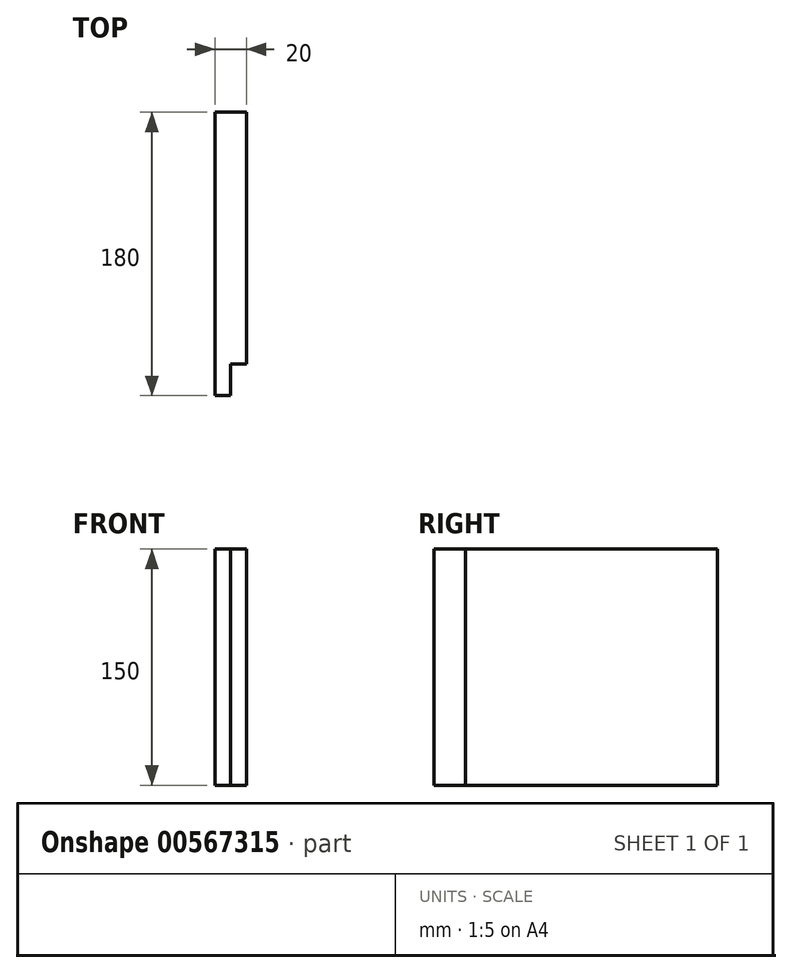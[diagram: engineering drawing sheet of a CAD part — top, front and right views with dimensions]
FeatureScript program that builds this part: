
annotation { "Feature Type Name" : "Feature", "Feature Type Description" : "" }
export const myFeature = defineFeature(function(context is Context, id is Id, definition is map)
    precondition{}
    {
        {
            var Q0;
            Q0=qCreatedBy(makeId("Right.planeOp"),FACE);
            var sketch = newSketch(context, id + "F0", { "sketchPlane" : qUnion([Q0])});
            skLineSegment(sketch, "E0.bottom", {"start": v(-83.42, 106.9) * mm, "end": v(96.58, 106.9) * mm});
            skLineSegment(sketch, "E0.top", {"start": v(-83.42, -43.1) * mm, "end": v(96.58, -43.1) * mm});
            skLineSegment(sketch, "E0.left", {"start": v(-83.42, 106.9) * mm, "end": v(-83.42, -43.1) * mm});
            skLineSegment(sketch, "E0.right", {"start": v(96.58, 106.9) * mm, "end": v(96.58, -43.1) * mm});
            skSolve(sketch);
        }
        {
            var Q0;
            Q0 = qSketchRegion(id + "F0", true);
            extrude(context, id + "F1", {"entities" : qUnion([Q0]), "depth" : 20 * mm, "offsetDistance" : 25 * mm});
        }
        {
            var Q0;
            Q0=makeQuery(id+"F1.opExtrude","SWEPT_FACE",FACE,{"disambiguationData":[OSD([sQuery(id+"F0.wireOp",EDGE,"E0.left")])]});
            var sketch = newSketch(context, id + "F2", { "sketchPlane" : qUnion([Q0])});
            skLineSegment(sketch, "E1", {"start": v(10, 106.9) * mm, "end": v(10, -43.1) * mm});
            skSolve(sketch);
        }
        {
            var Q0;
            {var subQ0=sQuery(id+"F2.wireOp",EDGE,"E1");Q0=makeQuery(id+"F2.imprint","IMPRINT",FACE,{"disambiguationData":[TD([[makeQuery(id+"F2.imprint","IMPRINT",EDGE,{"derivedFrom":subQ0}),1.0]])]});}
            extrude(context, id + "F3", {"entities" : qUnion([Q0]), "operationType" : NewBodyOperationType.REMOVE, "oppositeDirection" : true, "depth" : 20 * mm, "offsetDistance" : 25 * mm});
        }
        {
            var Q0;
            Q0=makeQuery(id+"F1.opExtrude","SWEPT_FACE",FACE,{"disambiguationData":[OSD([sQuery(id+"F0.wireOp",EDGE,"E0.right")])]});
            var sketch = newSketch(context, id + "F4", { "sketchPlane" : qUnion([Q0])});
            skLineSegment(sketch, "E2", {"start": v(-20, 31.9) * mm, "end": v(0, 31.9) * mm});
            skCircle(sketch, "E3", {"center": v(-10, 31.9) * mm, "radius": 4 * mm});
            skLineSegment(sketch, "E4", {"start": v(-20, 66.9) * mm, "end": v(0, 66.9) * mm});
            skLineSegment(sketch, "E5", {"start": v(-20, -3.1) * mm, "end": v(0, -3.1) * mm});
            skCircle(sketch, "E6", {"center": v(-10, 66.9) * mm, "radius": 4 * mm});
            skCircle(sketch, "E7", {"center": v(-10, -3.1) * mm, "radius": 4 * mm});
            skSolve(sketch);
        }
        {
            var Q0;
            Q0=sQuery(id+"F4.wireOp",EDGE,"E6");
            var Q1;
            Q1=sQuery(id+"F4.wireOp",EDGE,"E3");
            var Q2;
            Q2=sQuery(id+"F4.wireOp",EDGE,"E7");
            extrude(context, id + "F5", {"bodyType" : ToolBodyType.SURFACE, "surfaceEntities" : qUnion([Q0, Q1, Q2]), "oppositeDirection" : true, "depth" : 10 * mm, "offsetDistance" : 25 * mm});
        }
    });
